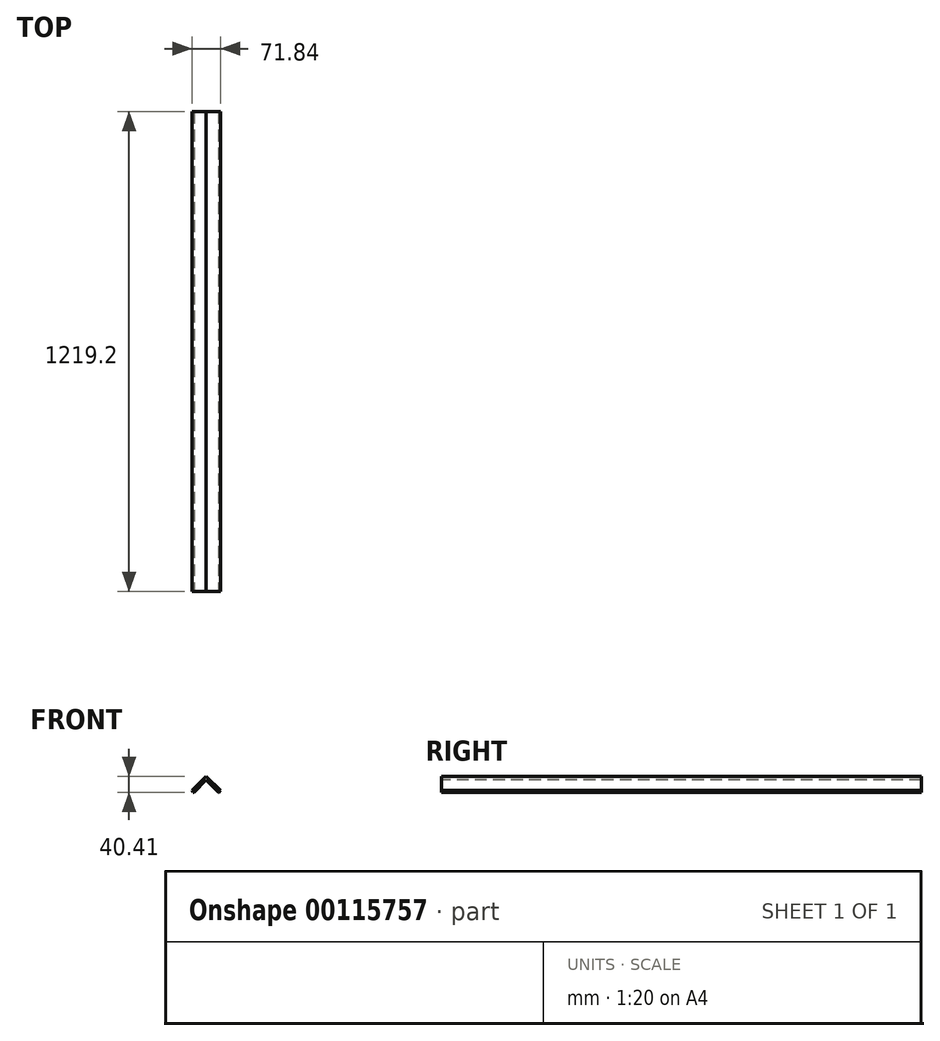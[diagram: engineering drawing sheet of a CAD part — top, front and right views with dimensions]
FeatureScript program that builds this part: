
annotation { "Feature Type Name" : "Feature", "Feature Type Description" : "" }
export const myFeature = defineFeature(function(context is Context, id is Id, definition is map)
    precondition{}
    {
        {
            var Q0;
            Q0=qCreatedBy(makeId("Front.planeOp"),FACE);
            var sketch = newSketch(context, id + "F0", { "sketchPlane" : qUnion([Q0])});
            skLineSegment(sketch, "E0", {"start": v(0, 0) * mm, "end": v(35.92, 35.92) * mm});
            skLineSegment(sketch, "E1", {"start": v(35.92, 35.92) * mm, "end": v(71.84, 0) * mm});
            skLineSegment(sketch, "E2.0", {"start": v(35.92, 26.94) * mm, "end": v(67.35, -4.5) * mm});
            skLineSegment(sketch, "E2.1", {"start": v(4.5, -4.5) * mm, "end": v(35.92, 26.94) * mm});
            skLineSegment(sketch, "E3", {"start": v(4.5, -4.5) * mm, "end": v(2.9, -4.5) * mm});
            skLineSegment(sketch, "E4", {"start": v(67.35, -4.5) * mm, "end": v(68.94, -4.5) * mm});
            skLineSegment(sketch, "E5", {"start": v(2.9, -4.5) * mm, "end": v(0, 0) * mm});
            skLineSegment(sketch, "E6", {"start": v(68.94, -4.5) * mm, "end": v(71.84, 0) * mm});
            skSolve(sketch);
        }
        {
            var Q0;
            Q0 = qSketchRegion(id + "F0", true);
            extrude(context, id + "F1", {"entities" : qUnion([Q0]), "oppositeDirection" : true, "depth" : 1219.2 * mm});
        }
    });
